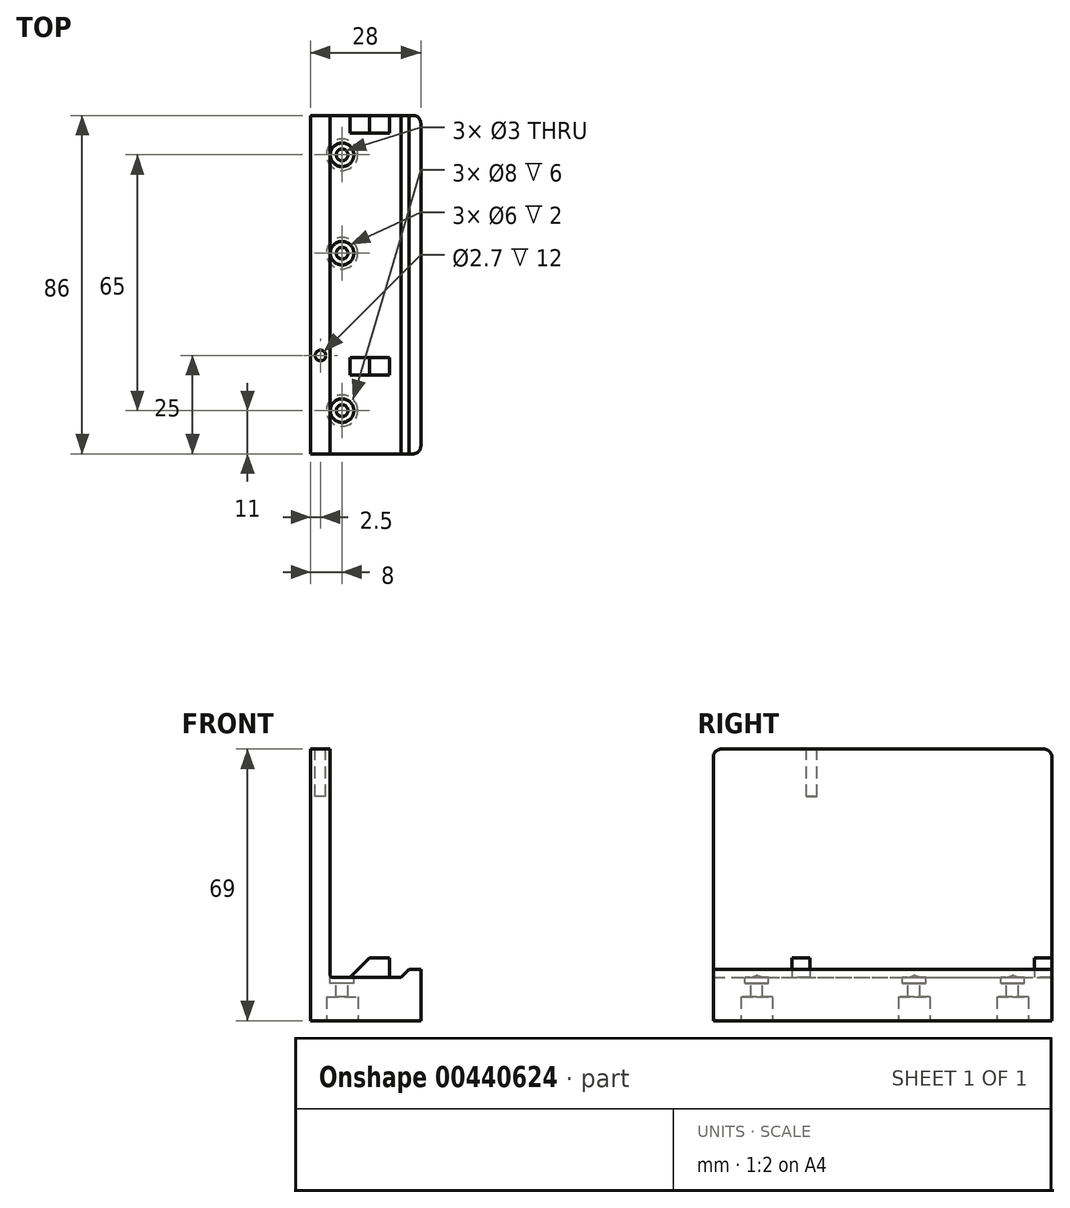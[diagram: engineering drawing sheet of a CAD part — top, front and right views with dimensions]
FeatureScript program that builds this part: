
annotation { "Feature Type Name" : "Feature", "Feature Type Description" : "" }
export const myFeature = defineFeature(function(context is Context, id is Id, definition is map)
    precondition{}
    {
        {
            var Q0;
            Q0=qCreatedBy(makeId("Front.planeOp"),FACE);
            var sketch = newSketch(context, id + "F0", { "sketchPlane" : qUnion([Q0])});
            skLineSegment(sketch, "E0", {"start": v(0, 69) * mm, "end": v(0, 11.5) * mm});
            skLineSegment(sketch, "E1", {"start": v(0, 69) * mm, "end": v(-5, 69) * mm});
            skLineSegment(sketch, "E2", {"start": v(-5, 69) * mm, "end": v(-5, 0) * mm});
            skLineSegment(sketch, "E3", {"start": v(-5, 0) * mm, "end": v(23, 0) * mm});
            skLineSegment(sketch, "E4", {"start": v(0.5, 11) * mm, "end": v(18, 11) * mm});
            skPoint(sketch, "E5.visualSharp", {"position": v(0, 11) * mm});
            skArc(sketch, "E5.filletArc", {"start": v(0, 11.5) * mm, "mid": v(0.15, 11.15) * mm, "end": v(0.5, 11) * mm});
            skLineSegment(sketch, "E6", {"start": v(20, 13) * mm, "end": v(23, 13) * mm});
            skLineSegment(sketch, "E7", {"start": v(23, 13) * mm, "end": v(23, 0) * mm});
            skLineSegment(sketch, "E8", {"start": v(18, 11) * mm, "end": v(20, 13) * mm});
            skSolve(sketch);
        }
        {
            var Q0;
            Q0 = qSketchRegion(id + "F0", true);
            extrude(context, id + "F1", {"entities" : qUnion([Q0]), "endBound" : BoundingType.SYMMETRIC, "depth" : 86 * mm});
        }
        {
            var Q0;
            Q0=makeQuery(id+"F1.opExtrude","SWEPT_FACE",FACE,{"disambiguationData":[OSD([sQuery(id+"F0.wireOp",EDGE,"E3")])]});
            var sketch = newSketch(context, id + "F2", { "sketchPlane" : qUnion([Q0])});
            skCircle(sketch, "E9", {"center": v(3, -33) * mm, "radius": 4 * mm});
            skCircle(sketch, "E10", {"center": v(3, -8) * mm, "radius": 4 * mm});
            skCircle(sketch, "E11", {"center": v(3, 32) * mm, "radius": 4 * mm});
            skLineSegment(sketch, "E12", {"start": v(3, -46.09) * mm, "end": v(3, 49.3) * mm, "construction": true});
            skLineSegment(sketch, "E13", {"start": v(-6.86, -33) * mm, "end": v(12.39, -33) * mm, "construction": true});
            skLineSegment(sketch, "E14", {"start": v(-7.6, -8) * mm, "end": v(13.66, -8) * mm, "construction": true});
            skLineSegment(sketch, "E15", {"start": v(-7.39, 32) * mm, "end": v(13.66, 32) * mm, "construction": true});
            skSolve(sketch);
        }
        {
            var Q0;
            Q0 = qSketchRegion(id + "F2", true);
            extrude(context, id + "F3", {"entities" : qUnion([Q0]), "operationType" : NewBodyOperationType.REMOVE, "oppositeDirection" : true, "depth" : 6 * mm});
        }
        {
            var Q0;
            Q0=makeQuery(id+"F1.opExtrude","SWEPT_FACE",FACE,{"disambiguationData":[OSD([sQuery(id+"F0.wireOp",EDGE,"E4")])]});
            var sketch = newSketch(context, id + "F4", { "sketchPlane" : qUnion([Q0])});
            skCircle(sketch, "E16", {"center": v(3, 33) * mm, "radius": 1.5 * mm});
            skCircle(sketch, "E17", {"center": v(3, 8) * mm, "radius": 1.5 * mm});
            skCircle(sketch, "E18", {"center": v(3, -32) * mm, "radius": 1.5 * mm});
            skCircle(sketch, "E19", {"center": v(3, 8) * mm, "radius": 3 * mm});
            skCircle(sketch, "E20", {"center": v(3, 33) * mm, "radius": 3 * mm});
            skCircle(sketch, "E21", {"center": v(3, -32) * mm, "radius": 3 * mm});
            skSolve(sketch);
        }
        {
            var Q0;
            Q0=makeQuery(id+"F4.imprint","IMPRINT",FACE,{"disambiguationData":[TD([[makeQuery(id+"F4.imprint","IMPRINT",EDGE,{"derivedFrom":sQuery(id+"F4.wireOp",EDGE,"E16")}),1.0]])]});
            var Q1;
            Q1=makeQuery(id+"F4.imprint","IMPRINT",FACE,{"disambiguationData":[TD([[makeQuery(id+"F4.imprint","IMPRINT",EDGE,{"derivedFrom":sQuery(id+"F4.wireOp",EDGE,"E17")}),1.0]])]});
            var Q2;
            Q2=makeQuery(id+"F4.imprint","IMPRINT",FACE,{"disambiguationData":[TD([[makeQuery(id+"F4.imprint","IMPRINT",EDGE,{"derivedFrom":sQuery(id+"F4.wireOp",EDGE,"E18")}),1.0]])]});
            extrude(context, id + "F5", {"entities" : qUnion([Q0, Q1, Q2]), "operationType" : NewBodyOperationType.REMOVE, "oppositeDirection" : true, "depth" : 25 * mm});
        }
        {
            var Q0;
            Q0 = qSketchRegion(id + "F4", true);
            extrude(context, id + "F6", {"entities" : qUnion([Q0]), "operationType" : NewBodyOperationType.REMOVE, "endBound" : BoundingType.SYMMETRIC, "oppositeDirection" : true, "depth" : 3 * mm});
        }
        {
            var Q0;
            {var subQ1=sQuery(id+"F0.wireOp",EDGE,"E4");var subQ11=makeQuery(id+"F1.opExtrude","CAP_EDGE",EDGE,{"disambiguationData":[OSD([subQ1])],"isStart":true});Q0=makeQuery(id+"F4.imprint","IMPRINT",FACE,{"disambiguationData":[TD([[makeQuery(id+"F4.imprint","IMPRINT",EDGE,{"derivedFrom":subQ11}),-1.0]])]});}
            var sketch = newSketch(context, id + "F7", { "sketchPlane" : qUnion([Q0])});
            skLineSegment(sketch, "E22.bottom", {"start": v(5, 43) * mm, "end": v(15, 43) * mm});
            skLineSegment(sketch, "E22.top", {"start": v(5, 38.5) * mm, "end": v(15, 38.5) * mm});
            skLineSegment(sketch, "E22.left", {"start": v(5, 43) * mm, "end": v(5, 38.5) * mm});
            skLineSegment(sketch, "E22.right", {"start": v(15, 43) * mm, "end": v(15, 38.5) * mm});
            skLineSegment(sketch, "E23.bottom", {"start": v(5.02, -63.53) * mm, "end": v(22.73, -63.53) * mm, "construction": true});
            skLineSegment(sketch, "E23.top", {"start": v(5.02, -71.82) * mm, "end": v(22.73, -71.82) * mm, "construction": true});
            skLineSegment(sketch, "E23.left", {"start": v(5.02, -63.53) * mm, "end": v(5.02, -71.82) * mm, "construction": true});
            skLineSegment(sketch, "E23.right", {"start": v(22.73, -63.53) * mm, "end": v(22.73, -71.82) * mm, "construction": true});
            skLineSegment(sketch, "E24.bottom", {"start": v(5, -18.5) * mm, "end": v(15, -18.5) * mm});
            skLineSegment(sketch, "E24.top", {"start": v(5, -23) * mm, "end": v(15, -23) * mm});
            skLineSegment(sketch, "E24.left", {"start": v(5, -18.5) * mm, "end": v(5, -23) * mm});
            skLineSegment(sketch, "E24.right", {"start": v(15, -18.5) * mm, "end": v(15, -23) * mm});
            skSolve(sketch);
        }
        {
            var Q0;
            Q0 = qSketchRegion(id + "F7", true);
            extrude(context, id + "F8", {"entities" : qUnion([Q0]), "operationType" : NewBodyOperationType.ADD, "depth" : 5 * mm});
        }
        {
            var Q0;
            Q0=qCreatedBy(makeId("Front.planeOp"),FACE);
            var sketch = newSketch(context, id + "F9", { "sketchPlane" : qUnion([Q0])});
            skLineSegment(sketch, "E25", {"start": v(5, 11) * mm, "end": v(13, 19) * mm});
            skLineSegment(sketch, "E26", {"start": v(13, 19) * mm, "end": v(5, 19) * mm});
            skLineSegment(sketch, "E27", {"start": v(5, 19) * mm, "end": v(5, 11) * mm});
            skSolve(sketch);
        }
        {
            var Q0;
            Q0 = qSketchRegion(id + "F9", true);
            extrude(context, id + "F10", {"entities" : qUnion([Q0]), "operationType" : NewBodyOperationType.REMOVE, "endBound" : BoundingType.SYMMETRIC, "oppositeDirection" : true, "depth" : 100 * mm});
        }
        {
            var Q0;
            Q0=makeQuery(id+"F1.opExtrude","CAP_EDGE",EDGE,{"disambiguationData":[OSD([sQuery(id+"F0.wireOp",EDGE,"E7")])],"isStart":false});
            var Q1;
            Q1=makeQuery(id+"F1.opExtrude","CAP_EDGE",EDGE,{"disambiguationData":[OSD([sQuery(id+"F0.wireOp",EDGE,"E7")])],"isStart":true});
            var Q2;
            Q2=makeQuery(id+"F1.opExtrude","CAP_EDGE",EDGE,{"disambiguationData":[OSD([sQuery(id+"F0.wireOp",EDGE,"E1")])],"isStart":false});
            var Q3;
            Q3=makeQuery(id+"F1.opExtrude","CAP_EDGE",EDGE,{"disambiguationData":[OSD([sQuery(id+"F0.wireOp",EDGE,"E1")])],"isStart":true});
            fillet(context, id + "F11", {"entities" : qUnion([Q0, Q1, Q2, Q3]), "radius" : 2 * mm, "tangentPropagation" : true, "defaultsChanged" : false, "vertexSettings" : [], "allowEdgeOverflow" : false});
        }
        {
            var Q0;
            Q0=makeQuery(id+"F1.opExtrude","SWEPT_FACE",FACE,{"disambiguationData":[OSD([sQuery(id+"F0.wireOp",EDGE,"E0")])]});
            var sketch = newSketch(context, id + "F12", { "sketchPlane" : qUnion([Q0])});
            skCircle(sketch, "E28", {"center": v(-21, 65.5) * mm, "radius": 1.05 * mm});
            skCircle(sketch, "E29", {"center": v(37, 65.5) * mm, "radius": 1.05 * mm});
            skLineSegment(sketch, "E30", {"start": v(-78.47, 65.5) * mm, "end": v(85.51, 65.5) * mm, "construction": true});
            skLineSegment(sketch, "E31", {"start": v(8, 86.48) * mm, "end": v(8, -9.36) * mm, "construction": true});
            skSolve(sketch);
        }
        {
            var Q0;
            Q0=makeQuery(id+"F1.opExtrude","SWEPT_FACE",FACE,{"disambiguationData":[OSD([sQuery(id+"F0.wireOp",EDGE,"E1")])]});
            var sketch = newSketch(context, id + "F13", { "sketchPlane" : qUnion([Q0])});
            skCircle(sketch, "E32", {"center": v(-2.5, -18) * mm, "radius": 1.35 * mm});
            skLineSegment(sketch, "E33", {"start": v(0, -18) * mm, "end": v(-5, -18) * mm, "construction": true});
            skLineSegment(sketch, "E34", {"start": v(-5, 11) * mm, "end": v(0, 11) * mm, "construction": true});
            skSolve(sketch);
        }
        {
            var Q0;
            Q0=makeQuery(id+"F13.imprint","IMPRINT",FACE,{"disambiguationData":[TD([[makeQuery(id+"F13.imprint","IMPRINT",EDGE,{"derivedFrom":sQuery(id+"F13.wireOp",EDGE,"E32")}),1.0]])]});
            extrude(context, id + "F14", {"entities" : qUnion([Q0]), "operationType" : NewBodyOperationType.REMOVE, "oppositeDirection" : true, "depth" : 12 * mm, "offsetDistance" : 25 * mm});
        }
    });
